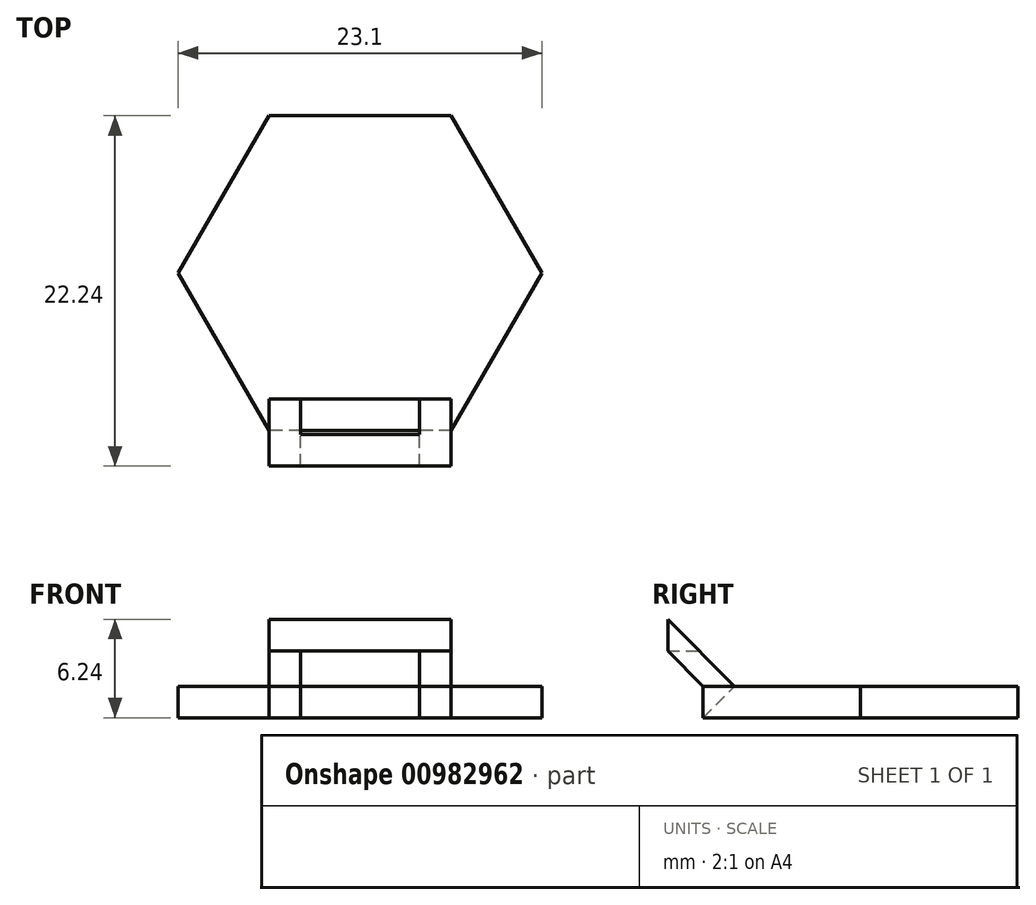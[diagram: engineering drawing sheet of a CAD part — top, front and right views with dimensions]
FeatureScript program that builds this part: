
annotation { "Feature Type Name" : "Feature", "Feature Type Description" : "" }
export const myFeature = defineFeature(function(context is Context, id is Id, definition is map)
    precondition{}
    {
        {
            var Q0;
            Q0=qCreatedBy(makeId("Top.planeOp"),FACE);
            var sketch = newSketch(context, id + "F0", { "sketchPlane" : qUnion([Q0])});
            skCircle(sketch, "E0.cCircle", {"center": v(0, 0) * mm, "radius": 10 * mm, "construction": true});
            skLineSegment(sketch, "E0.0", {"start": v(5.77, -10) * mm, "end": v(-5.77, -10) * mm});
            skLineSegment(sketch, "E0.1", {"start": v(-5.77, -10) * mm, "end": v(-11.55, 0) * mm});
            skLineSegment(sketch, "E0.2", {"start": v(-11.55, 0) * mm, "end": v(-5.77, 10) * mm});
            skLineSegment(sketch, "E0.3", {"start": v(-5.77, 10) * mm, "end": v(5.77, 10) * mm});
            skLineSegment(sketch, "E0.4", {"start": v(5.77, 10) * mm, "end": v(11.55, 0) * mm});
            skLineSegment(sketch, "E0.5", {"start": v(11.55, 0) * mm, "end": v(5.77, -10) * mm});
            skPoint(sketch, "E0.0.midPoint", {"position": v(0, -10) * mm});
            skLineSegment(sketch, "E1", {"start": v(-5.77, -10) * mm, "end": v(-3.77, -10) * mm});
            skLineSegment(sketch, "E2", {"start": v(-6.77, -8.27) * mm, "end": v(-5.77, -10) * mm});
            skLineSegment(sketch, "E3", {"start": v(-5.77, -10) * mm, "end": v(-5.77, -5.73) * mm});
            skLineSegment(sketch, "E4", {"start": v(5.77, -10) * mm, "end": v(5.77, -5.53) * mm});
            skLineSegment(sketch, "E5", {"start": v(0, 10) * mm, "end": v(0, 8) * mm});
            skSolve(sketch);
        }
        {
            var Q0;
            Q0 = qSketchRegion(id + "F0", true);
            extrude(context, id + "F1", {"entities" : qUnion([Q0]), "oppositeDirection" : true, "depth" : 2 * mm, "offsetDistance" : 25 * mm});
        }
        {
            var Q0;
            Q0=sQuery(id+"F0.wireOp",EDGE,"E3");
            extrude(context, id + "F2", {"bodyType" : ToolBodyType.SURFACE, "surfaceEntities" : qUnion([Q0]), "depth" : 2 * mm, "offsetDistance" : 25 * mm});
        }
        {
            var Q0;
            Q0=makeQuery(id+"F2.opExtrude","SWEPT_FACE",FACE,{"disambiguationData":[OSD([sQuery(id+"F0.wireOp",EDGE,"E3")])]});
            var sketch = newSketch(context, id + "F3", { "sketchPlane" : qUnion([Q0])});
            skLineSegment(sketch, "E6", {"start": v(-10, 0) * mm, "end": v(-8, 0) * mm});
            skLineSegment(sketch, "E7", {"start": v(-8, 0) * mm, "end": v(-12.24, 4.24) * mm});
            skLineSegment(sketch, "E8", {"start": v(-12.24, 4.24) * mm, "end": v(-12.24, 2.24) * mm});
            skLineSegment(sketch, "E9", {"start": v(-12.24, 2.24) * mm, "end": v(-10, 0) * mm});
            skSolve(sketch);
        }
        {
            var Q0;
            {var subQ0=sQuery(id+"F3.wireOp",EDGE,"E6");Q0=makeQuery(id+"F3.imprint","IMPRINT",FACE,{"disambiguationData":[TD([[makeQuery(id+"F3.imprint","IMPRINT",EDGE,{"derivedFrom":subQ0}),1.0]])]});}
            var Q1;
            {var subQ2=sQuery(id+"F3.wireOp",EDGE,"E8");Q1=makeQuery(id+"F3.imprint","IMPRINT",FACE,{"disambiguationData":[TD([[makeQuery(id+"F3.imprint","IMPRINT",EDGE,{"derivedFrom":subQ2}),1.0]])]});}
            extrude(context, id + "F4", {"entities" : qUnion([Q0, Q1]), "operationType" : NewBodyOperationType.ADD, "depth" : 11.55 * mm, "offsetDistance" : 25 * mm});
        }
        {
            var Q0;
            Q0=makeQuery(id+"F4.opExtrude","SWEPT_FACE",FACE,{"disambiguationData":[OSD([sQuery(id+"F3.wireOp",EDGE,"E7")])]});
            var sketch = newSketch(context, id + "F5", { "sketchPlane" : qUnion([Q0])});
            skLineSegment(sketch, "E10", {"start": v(-5.77, 11.66) * mm, "end": v(-3.77, 11.66) * mm});
            skLineSegment(sketch, "E11", {"start": v(5.77, 11.66) * mm, "end": v(3.77, 11.66) * mm});
            skLineSegment(sketch, "E12", {"start": v(-3.77, 11.66) * mm, "end": v(-3.77, 5.66) * mm});
            skLineSegment(sketch, "E13", {"start": v(3.77, 11.66) * mm, "end": v(3.77, 5.66) * mm});
            skSolve(sketch);
        }
        {
            var Q0;
            {var subQ0=sQuery(id+"F5.wireOp",EDGE,"E12");Q0=makeQuery(id+"F5.imprint","IMPRINT",FACE,{"disambiguationData":[TD([[makeQuery(id+"F5.imprint","IMPRINT",EDGE,{"derivedFrom":subQ0}),1.0]])]});}
            extrude(context, id + "F6", {"entities" : qUnion([Q0]), "operationType" : NewBodyOperationType.REMOVE, "oppositeDirection" : true, "depth" : 25 * mm, "offsetDistance" : 25 * mm});
        }
        {
            var Q0;
            Q0=makeQuery(id+"F6.boolean.opBoolean","COPY",FACE,{"derivedFrom":makeQuery(id+"F6.opExtrude","SWEPT_FACE",FACE,{"disambiguationData":[OSD([sQuery(id+"F5.wireOp",EDGE,"E13")])]})});
            var sketch = newSketch(context, id + "F7", { "sketchPlane" : qUnion([Q0])});
            skLineSegment(sketch, "E14", {"start": v(-12.24, 2.24) * mm, "end": v(-10.24, 2.24) * mm});
            skSolve(sketch);
        }
        {
            var Q0;
            {var subQ0=sQuery(id+"F7.wireOp",EDGE,"E14");Q0=makeQuery(id+"F7.imprint","IMPRINT",FACE,{"disambiguationData":[TD([[makeQuery(id+"F7.imprint","IMPRINT",EDGE,{"derivedFrom":subQ0}),1.0]])]});}
            var Q1;
            Q1=makeQuery(id+"F6.boolean.opBoolean","COPY",FACE,{"derivedFrom":makeQuery(id+"F6.opExtrude","SWEPT_FACE",FACE,{"disambiguationData":[OSD([sQuery(id+"F5.wireOp",EDGE,"E12")])]})});
            extrude(context, id + "F8", {"entities" : qUnion([Q0]), "operationType" : NewBodyOperationType.ADD, "endBound" : BoundingType.UP_TO_SURFACE, "depth" : 25 * mm, "endBoundEntityFace" : qUnion([Q1]), "offsetDistance" : 25 * mm});
        }
        {
            var Q0;
            Q0=sQuery(id+"F0.wireOp",EDGE,"E5");
            extrude(context, id + "F9", {"bodyType" : ToolBodyType.SURFACE, "surfaceEntities" : qUnion([Q0]), "depth" : 2 * mm, "offsetDistance" : 25 * mm});
        }
    });
